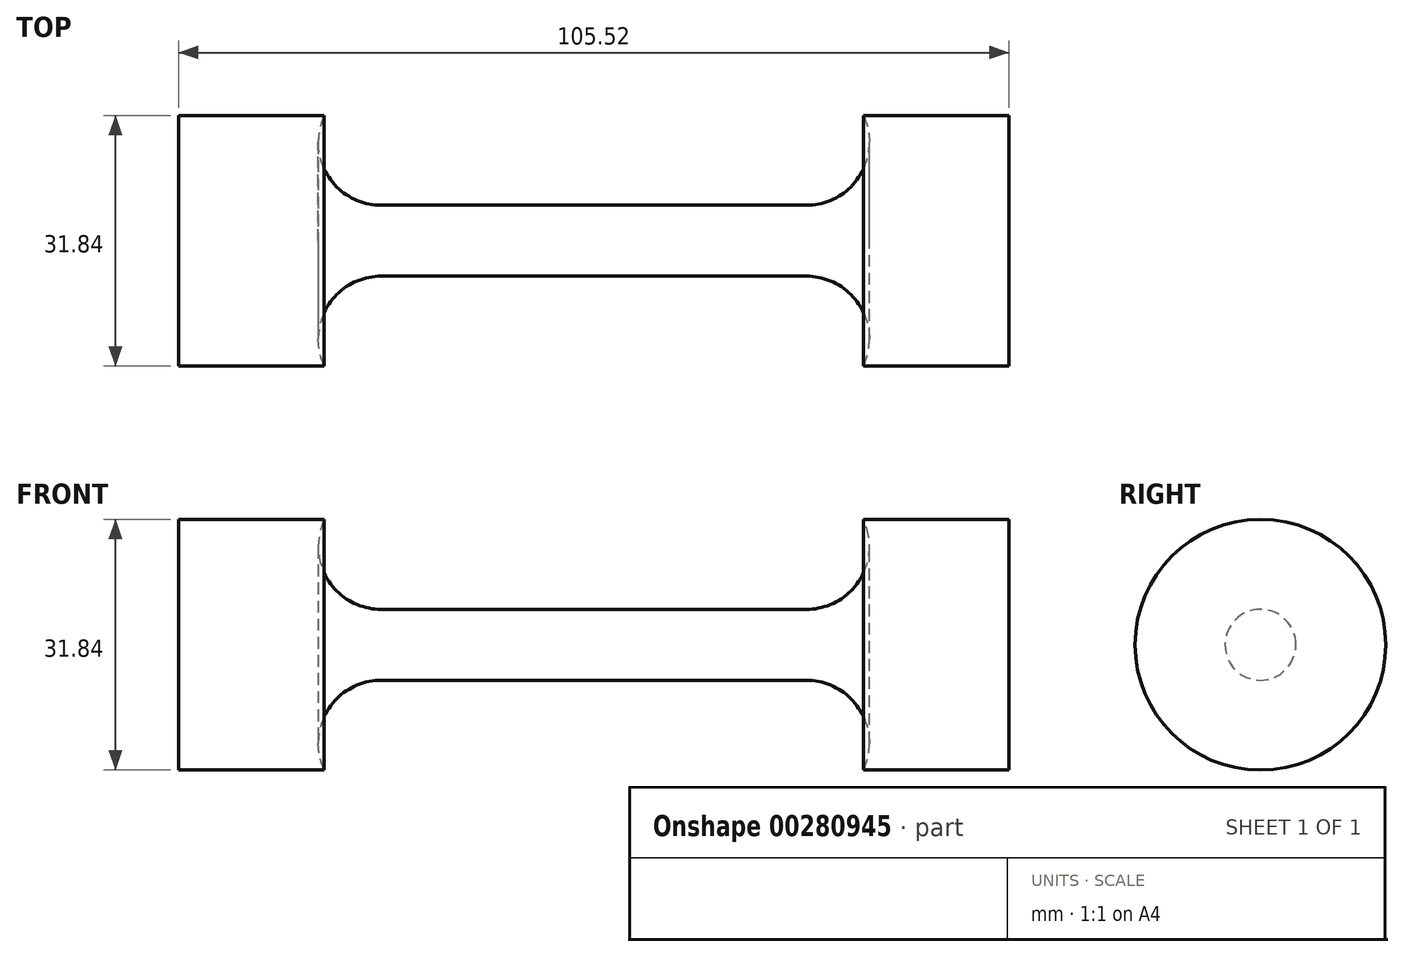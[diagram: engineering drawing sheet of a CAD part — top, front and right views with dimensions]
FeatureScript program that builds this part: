
annotation { "Feature Type Name" : "Feature", "Feature Type Description" : "" }
export const myFeature = defineFeature(function(context is Context, id is Id, definition is map)
    precondition{}
    {
        {
            var Q0;
            Q0=qCreatedBy(makeId("Front.planeOp"),FACE);
            var sketch = newSketch(context, id + "F0", { "sketchPlane" : qUnion([Q0])});
            skLineSegment(sketch, "E0", {"start": v(0, 4.5) * mm, "end": v(27, 4.5) * mm});
            skLineSegment(sketch, "E1", {"start": v(34.23, 15.92) * mm, "end": v(52.76, 15.92) * mm});
            skLineSegment(sketch, "E2", {"start": v(52.76, 0) * mm, "end": v(52.76, 15.92) * mm});
            skLineSegment(sketch, "E3", {"start": v(52.76, 0) * mm, "end": v(0, 0) * mm});
            skArc(sketch, "E4", {"start": v(27, 4.5) * mm, "mid": v(33.76, 8.22) * mm, "end": v(34.23, 15.92) * mm});
            skArc(sketch, "E5.MirrorCS", {"start": v(-27, 4.5) * mm, "mid": v(-33.76, 8.22) * mm, "end": v(-34.23, 15.92) * mm});
            skLineSegment(sketch, "E6.MirrorCS", {"start": v(0, 4.5) * mm, "end": v(-27, 4.5) * mm});
            skLineSegment(sketch, "E7.MirrorCS", {"start": v(-52.76, 0) * mm, "end": v(-52.76, 15.92) * mm});
            skLineSegment(sketch, "E8.MirrorCS", {"start": v(-52.76, 0) * mm, "end": v(0, 0) * mm});
            skLineSegment(sketch, "E9.MirrorCS", {"start": v(-34.23, 15.92) * mm, "end": v(-52.76, 15.92) * mm});
            skSolve(sketch);
        }
        {
            var Q0;
            Q0=makeQuery(id+"F0.imprint","IMPRINT",FACE,{"disambiguationData":[TD([[makeQuery(id+"F0.imprint","IMPRINT",EDGE,{"derivedFrom":sQuery(id+"F0.wireOp",EDGE,"E0")}),-1.0]])]});
            var Q1;
            Q1=sQuery(id+"F0.wireOp",EDGE,"E8.MirrorCS");
            revolve(context, id + "F1", {"entities" : qUnion([Q0]), "axis" : qUnion([Q1]), "revolveType" : RevolveType.FULL});
        }
    });
